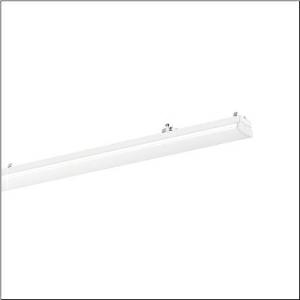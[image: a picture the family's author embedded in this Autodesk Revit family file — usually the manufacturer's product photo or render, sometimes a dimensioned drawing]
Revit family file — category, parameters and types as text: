
# Revit family: licross_r__11_recessed_opal_mo_51te1ddn46xg_40cb
name_source: partatom
category: Lighting Fixtures
units: mm (PartAtom-declared; Revit-internal decimal feet)

## family parameters
Cut with Voids When Loaded = No
Host = Face
Light Source = No
Part Type = Normal
Room Calculation Point = No
Round Connector Dimension = Use Diameter
Shared = No

## types (1)
- --- (1 x LED, 6320 lm, 35.2 W, 4000K)
    Apparent Load = 35 VA
    CIE Flux Codes = 44 73 91 87 100
    Color Rendering = 80
    Color Temperature = 4000K
    Default Elevation = 1800 mm
    Description = Licross® 11 recessed opal MO, luminaire insert, of sheet steel, coil coated, white, length: 1.500mm, width: 76mm, height: 87mm, LED rated luminous flux: 6.320lm, light colour: 840, control gear: DALI 2, with plug, 5-pole, with phase selection, mains connection: 220..240V, AC, 50/60Hz, rated input power: 35W, halogen-free wiring, primary optical cover: cover, of PMMA, light emission: direct with ceiling illumination distribution, primary light characteristic: symmetric, protection rating (complete): IP54, insulation class (complete): insulation class I (protective earthing), certification: CE, ENEC, VDE, UKCA, protection symbol: D if used in an environment with non-conductive dust loads with corresponding accessories, impact resistance: IK06, permissible ambient temperature for indoor applications: -25..+40°C, corresponds to IFS (International Featured Standards) requirements for safety and quality in the food industry, reducing of maximum allowable ambient temperature of 5°C with ceiling mounting, LABS conformity tested according to VDMA 24364:2018-05, packaging unit: 1 piece
    Height = 83 mm
    Lamp = 1 x LED
    Lamp Light Flux = 6320 lm
    Lamp Power = 35.2 W
    Lamp count = 1
    Length = 1500 mm
    Luminous efficacy = 180 lm/W
    Manufacturer = Siteco
    ModVariant = No
    Model = 51TE1DDN46XG
    Mounting Place = Ceiling
    Mounting Type = Pendant
    Number of Poles = 1
    OnlyDefault = Yes
    Power Factor = 1
    Product Name = Licross® 11 recessed opal MO
    Product group = luminaire insert
    ProductGroupID = 902
    Protection Class = Protection class I
    Protection Degree = IP 54
    RLX_Detail_Level = 1
    RLX_Emergency_Light_Flux = 0 lm
    RLX_Emergency_Type = 0
    RLX_Emergency_Type_DB = No
    RlxData = <blob elided: 26681 chars, md5=33326c38>
    Socket = socket
    Standby Power = 0 W
    System Light Flux = 6320 lm
    System Power = 35 W
    Type Comments = factory setting: luminous flux: 100 % | dim-lin: 254 | 238 mA
    Type Image = l_1313666.jpg
    URL = http://relux.com
    VarID = @adj_075988
    Voltage = 0 V
    Weight = 0.00 kg
    Width = 76 mm

## geometry (parser evidence)
native form markers: Blend x4, Sweep x13
no freeform markers — native parametric forms only
